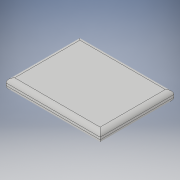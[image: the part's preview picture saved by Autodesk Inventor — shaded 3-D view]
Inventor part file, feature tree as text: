
AUTODESK INVENTOR PART (.ipt)
format: ipt  version: 2018 (Build 220112000, 112)  size: 103,424 bytes
history: native  units: in
note: dims shown in document units (in); Inventor stores cm internally (conversion verified against a paired STEP export)
features: extrude x1, fillet x1, sketch x1
ambient origin geometry x8: Origin, YZ Plane, XZ Plane, XY Plane, X Axis, Y Axis, Z Axis, Center Point
bodies: Solid1 (feature_tree)
feature tree (3):
  extrude  "Extrusion1"  Depth=2.5591in
  fillet  "Fillet1"  Radius=0.2992in
  sketch  "Sketch1"  dims[d0=2.0079in d1=2.5591in d2=0.2992in d3=0.0in d4=0.1181in]
